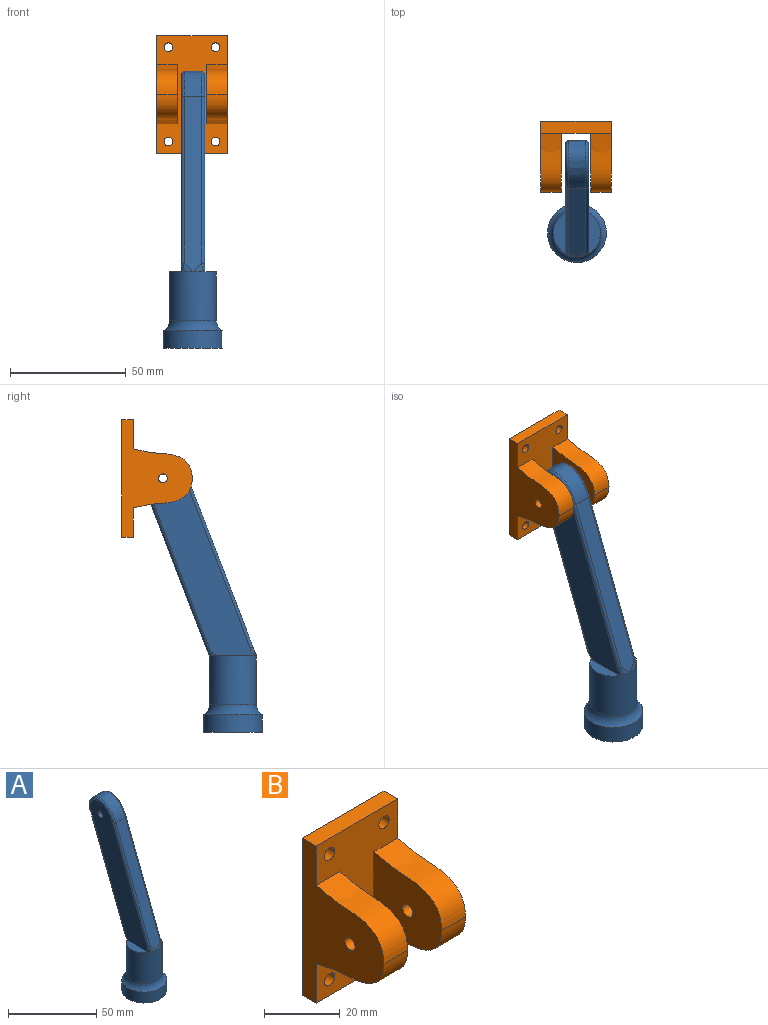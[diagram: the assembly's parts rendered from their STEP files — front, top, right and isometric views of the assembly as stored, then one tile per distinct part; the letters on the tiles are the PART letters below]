
ASSEMBLY  parts=2 mates=1
PART A: 26 faces, bbox 33.7x57.1x120.4 mm
  f0: plane 19.19x6.74mm, normal (0,0,1), area 63.8mm2, adj f1,f10,f16,f20
  f1: cylinder r=10.16mm len=21mm, axis (0,0,-1), area 1340.6mm2, adj f0,f2,f5,f12,f13,f14,f15
  f2: plane 19.19x6.74mm, normal (0,0,1), area 63.8mm2, adj f1,f11,f21,f25
  f3: cylinder r=12.7mm len=25.4mm, axis (0,0,1), area 608mm2, adj f4,f5
  f4: plane 25.4x25.4mm, normal (0,0,-1), area 506.7mm2, adj f3
  f5: torus R=15.24mm, axis (0,0,-1), area 369mm2, adj f1,f3
  f6: plane 75.85x29.21mm, normal (0,0.93,-0.36), area 608.2mm2, adj f7,f14,f15,f17,f22
  f7: extruded ~20.76x10.75mm, area 253.3mm2, adj f6,f8,f18,f23
  f8: plane 76.61x29.96mm, normal (0,-0.93,0.36), area 604.1mm2, adj f7,f12,f13,f19,f24
  f9: cylinder r=1.91mm len=10.16mm, axis (-1,0,0), area 121.6mm2, adj f10,f11
  f10: plane 85.35x46.59mm, normal (1,0,0), area 1452.2mm2, adj f0,f9,f16,f17,f18,f19,f20
  f11: plane 85.36x46.6mm, normal (-1,0,0), area 1452.2mm2, adj f2,f9,f21,f22,f23,f24,f25
  f12: bspline ~7.68x4.31mm, area 7mm2, adj f1,f8,f25
  f13: bspline ~7.68x4.31mm, area 7.4mm2, adj f1,f8,f20
  f14: bspline ~6.01x3.05mm, area 5mm2, adj f1,f6,f21
  f15: bspline ~6.01x3.05mm, area 5mm2, adj f1,f6,f16
  f16: bspline ~5.23x4.64mm, area 7.1mm2, adj f0,f10,f15,f17
  f17: cylinder r=1.27mm len=73.86mm, axis (0,-0.36,-0.93), area 156.9mm2, adj f6,f10,f16,f18
  f18: bspline ~25.47x23.45mm, area 63.4mm2, adj f7,f10,f17,f19
  f19: cylinder r=1.27mm len=72.49mm, axis (0,0.36,0.93), area 154mm2, adj f8,f10,f18,f20
  f20: bspline ~4.84x1.86mm, area 6.3mm2, adj f0,f10,f13,f19
  f21: bspline ~5.23x4.64mm, area 7.1mm2, adj f2,f11,f14,f22
  f22: cylinder r=1.27mm len=73.86mm, axis (0,0.36,0.93), area 156.9mm2, adj f6,f11,f21,f23
  f23: bspline ~25.47x23.46mm, area 63.4mm2, adj f7,f11,f22,f24
  f24: cylinder r=1.27mm len=72.49mm, axis (0,-0.36,-0.93), area 154mm2, adj f8,f11,f23,f25
  f25: bspline ~4.84x1.86mm, area 6.3mm2, adj f2,f11,f12,f24
PART B: 18 faces, bbox 30.5x30.5x50.8 mm
  f0: plane 50.8x30.48mm, normal (0,-1,0), area 1051.2mm2, adj f1,f2,f3,f4,f5,f6,f7,f8
  f1: plane 50.8x30.48mm, normal (1,0,0), area 759.1mm2, adj f0,f2,f7,f9,f10,f11,f12
  f2: plane 30.48x5.08mm, normal (0,0,1), area 154.8mm2, adj f0,f1,f3,f9
  f3: plane 50.8x30.48mm, normal (-1,0,0), area 759.1mm2, adj f0,f2,f7,f9,f14,f15,f16
  f4: cylinder r=1.91mm len=5.08mm, axis (0,1,0), area 60.8mm2, adj f0,f9
  f5: cylinder r=1.91mm len=5.08mm, axis (0,1,0), area 60.8mm2, adj f0,f9
  f6: cylinder r=1.91mm len=5.08mm, axis (0,1,0), area 60.8mm2, adj f0,f9
  f7: plane 30.48x5.08mm, normal (0,0,-1), area 154.8mm2, adj f0,f1,f3,f9
  f8: cylinder r=1.91mm len=5.08mm, axis (0,1,0), area 60.8mm2, adj f0,f9
  f9: plane 50.8x30.48mm, normal (0,1,0), area 1502.8mm2, adj f1,f2,f3,f4,f5,f6,f7,f8
  f10: extruded ~25.4x12.7mm, area 281.3mm2, adj f0,f1,f11,f13
  f11: extruded ~25.4x12.7mm, area 281.3mm2, adj f0,f1,f10,f13
  f12: cylinder r=1.91mm len=8.89mm, axis (1,0,0), area 106.4mm2, adj f1,f13
  f13: plane 25.4x25.4mm, normal (-1,0,0), area 501.1mm2, adj f0,f10,f11,f12
  f14: extruded ~25.4x12.7mm, area 281.3mm2, adj f0,f3,f15,f17
  f15: extruded ~25.4x12.7mm, area 281.3mm2, adj f0,f3,f14,f17
  f16: cylinder r=1.91mm len=8.89mm, axis (-1,0,0), area 106.4mm2, adj f3,f17
  f17: plane 25.4x25.4mm, normal (1,0,0), area 501.1mm2, adj f0,f14,f15,f16
PLACE A t=(-41.7,-9,10.28)mm
PLACE B t=(-42.1,39,112.28)mm
MATE cylindrical B.f12 <-> A.f9  axis (1,0,0) through (-26.86,21.22,112.28)mm
